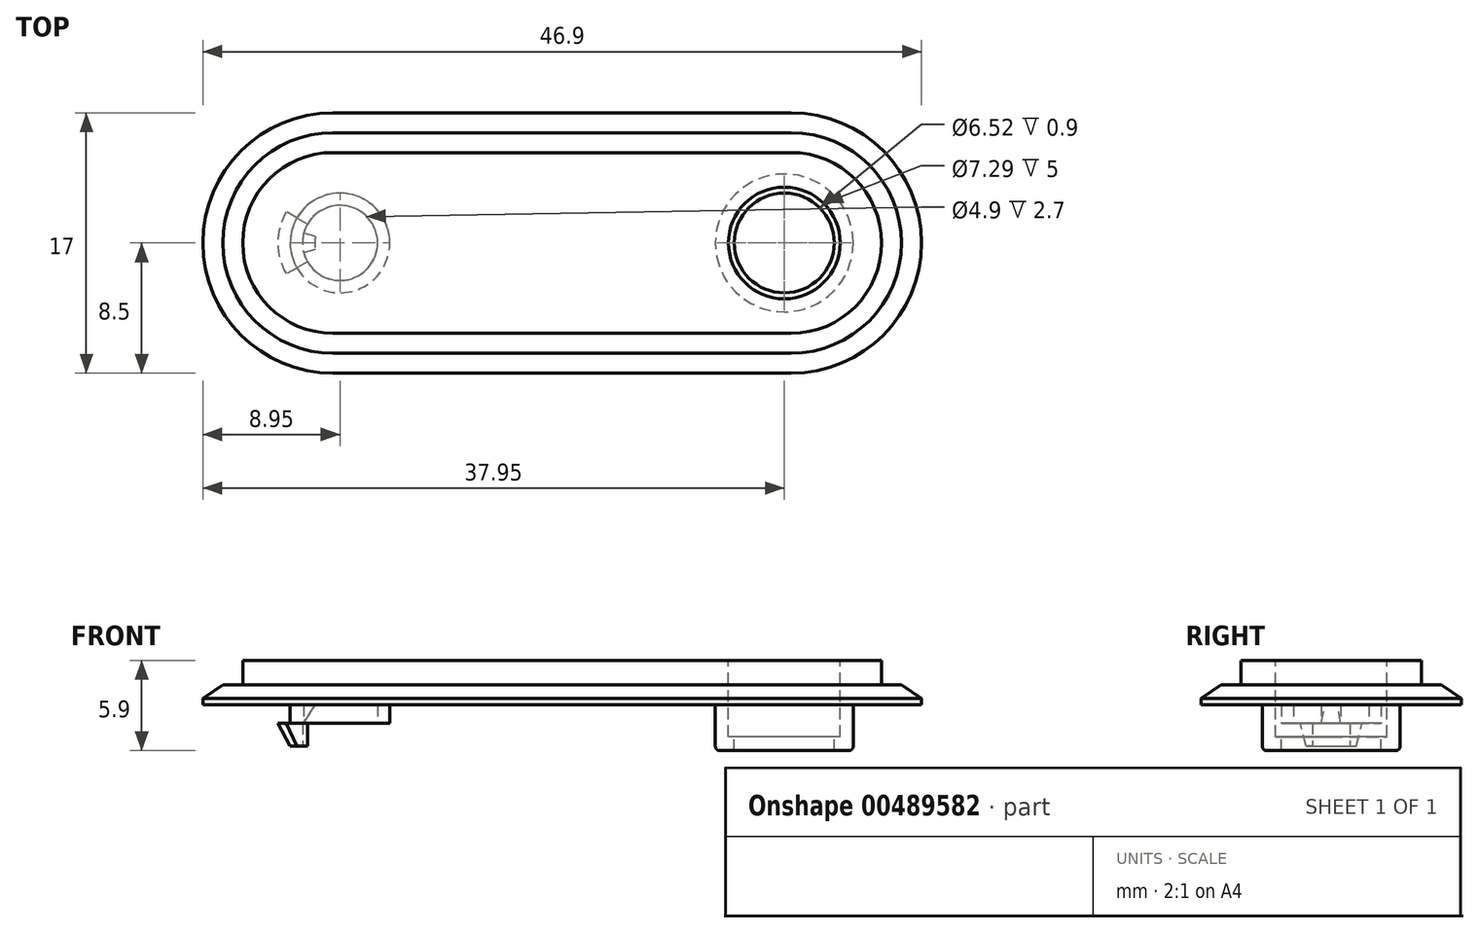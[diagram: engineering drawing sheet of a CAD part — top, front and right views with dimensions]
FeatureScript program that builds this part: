
annotation { "Feature Type Name" : "Feature", "Feature Type Description" : "" }
export const myFeature = defineFeature(function(context is Context, id is Id, definition is map)
    precondition{}
    {
        {
            var Q0;
            Q0=qCreatedBy(makeId("Top.planeOp"),FACE);
            var sketch = newSketch(context, id + "F0", { "sketchPlane" : qUnion([Q0])});
            skLineSegment(sketch, "E0.bottom", {"start": v(-14.95, 5.9) * mm, "end": v(14.95, 5.9) * mm});
            skLineSegment(sketch, "E0.top", {"start": v(-14.95, -5.9) * mm, "end": v(14.95, -5.9) * mm});
            skPoint(sketch, "E0.middle", {"position": v(0, 0) * mm});
            skPoint(sketch, "E1", {"position": v(-14.95, 0) * mm});
            skPoint(sketch, "E2", {"position": v(14.95, 0) * mm});
            skArc(sketch, "E3", {"start": v(-14.95, 5.9) * mm, "mid": v(-20.85, 0) * mm, "end": v(-14.95, -5.9) * mm});
            skArc(sketch, "E4", {"start": v(14.95, -5.9) * mm, "mid": v(20.85, 0) * mm, "end": v(14.95, 5.9) * mm});
            skPoint(sketch, "E5.orphan", {"position": v(-20.85, 5.9) * mm});
            skPoint(sketch, "E6.orphan", {"position": v(-20.85, -5.9) * mm});
            skPoint(sketch, "E7.orphan", {"position": v(20.85, 5.9) * mm});
            skPoint(sketch, "E8.orphan", {"position": v(20.85, -5.9) * mm});
            skPoint(sketch, "E9", {"position": v(-14.5, 0) * mm});
            skPoint(sketch, "E10", {"position": v(14.5, 0) * mm});
            skSolve(sketch);
        }
        {
            var Q0;
            Q0=makeQuery(id+"F0.imprint","IMPRINT",FACE,{"disambiguationData":[TD([[makeQuery(id+"F0.imprint","IMPRINT",EDGE,{"derivedFrom":sQuery(id+"F0.wireOp",EDGE,"E0.bottom")}),-1.0]])]});
            extrude(context, id + "F1", {"entities" : qUnion([Q0]), "depth" : 1.6 * mm});
        }
        {
            var Q0;
            Q0=qCreatedBy(makeId("Top.planeOp"),FACE);
            cPlane(context, id + "F2", {"entities" : qUnion([Q0]), "cplaneType" : CPlaneType.OFFSET, "offset" : 1.3 * mm, "oppositeDirection" : true, "width" : 150 * mm, "height" : 150 * mm});
        }
        {
            var Q0;
            Q0=qCreatedBy(id+"F2.planeOp",FACE);
            var sketch = newSketch(context, id + "F3", { "sketchPlane" : qUnion([Q0])});
            skPoint(sketch, "E11.middle", {"position": v(0, 0) * mm});
            skPoint(sketch, "E12", {"position": v(-14.95, 0) * mm});
            skPoint(sketch, "E13", {"position": v(14.95, 0) * mm});
            skPoint(sketch, "E14.orphan", {"position": v(-20.85, 5.9) * mm});
            skPoint(sketch, "E15.orphan", {"position": v(-20.85, -5.9) * mm});
            skPoint(sketch, "E16.orphan", {"position": v(20.85, 5.9) * mm});
            skPoint(sketch, "E17.orphan", {"position": v(20.85, -5.9) * mm});
            skLineSegment(sketch, "E18.0", {"start": v(-14.95, 8.5) * mm, "end": v(14.95, 8.5) * mm});
            skArc(sketch, "E18.1", {"start": v(-14.95, 8.5) * mm, "mid": v(-23.45, 0) * mm, "end": v(-14.95, -8.5) * mm});
            skLineSegment(sketch, "E18.2", {"start": v(-14.95, -8.5) * mm, "end": v(14.95, -8.5) * mm});
            skArc(sketch, "E18.3", {"start": v(14.95, -8.5) * mm, "mid": v(23.45, 0) * mm, "end": v(14.95, 8.5) * mm});
            skSolve(sketch);
        }
        {
            var Q0;
            Q0 = qSketchRegion(id + "F3", true);
            extrude(context, id + "F4", {"entities" : qUnion([Q0]), "operationType" : NewBodyOperationType.ADD, "depth" : 1.3 * mm});
        }
        {
            var Q0;
            Q0=makeQuery(id+"F4.opExtrude","CAP_EDGE",EDGE,{"disambiguationData":[OSD([sQuery(id+"F3.wireOp",EDGE,"E18.0")])],"isStart":false});
            var Q1;
            Q1=makeQuery(id+"F1.opExtrude","CAP_EDGE",EDGE,{"disambiguationData":[OSD([sQuery(id+"F0.wireOp",EDGE,"E0.top")])],"isStart":true});
            chamfer(context, id + "F5", {"entities" : qUnion([Q0, Q1]), "chamferType" : ChamferType.TWO_OFFSETS, "width1" : 0.9 * mm, "oppositeDirection" : false, "width2" : 1.3 * mm, "tangentPropagation" : true});
        }
        {
            var Q0;
            Q0=makeQuery(id+"F4.opExtrude","CAP_FACE",FACE,{"disambiguationData":[OSD([sQuery(id+"F3.wireOp",EDGE,"E18.0"),sQuery(id+"F3.wireOp",EDGE,"E18.1"),sQuery(id+"F3.wireOp",EDGE,"E18.2"),sQuery(id+"F3.wireOp",EDGE,"E18.3")])],"isStart":true});
            var sketch = newSketch(context, id + "F6", { "sketchPlane" : qUnion([Q0])});
            skCircle(sketch, "E19", {"center": v(14.5, 0) * mm, "radius": 4.5 * mm});
            skCircle(sketch, "E20", {"center": v(14.5, 0) * mm, "radius": 3.26 * mm});
            skSolve(sketch);
        }
        {
            var Q0;
            Q0=makeQuery(id+"F6.imprint","IMPRINT",FACE,{"disambiguationData":[TD([[makeQuery(id+"F6.imprint","IMPRINT",EDGE,{"derivedFrom":sQuery(id+"F6.wireOp",EDGE,"E19")}),1.0]])]});
            extrude(context, id + "F7", {"entities" : qUnion([Q0]), "operationType" : NewBodyOperationType.ADD, "depth" : 3 * mm});
        }
        {
            var Q0;
            Q0=makeQuery(id+"F7.boolean.opBoolean","SPLIT",FACE,{"disambiguationData":[TD([makeQuery(id+"F7.opExtrude","SWEPT_FACE",FACE,{"disambiguationData":[OSD([sQuery(id+"F6.wireOp",EDGE,"E20")])]})])],"derivedFrom":makeQuery(id+"F4.opExtrude","CAP_FACE",FACE,{"disambiguationData":[OSD([sQuery(id+"F3.wireOp",EDGE,"E18.0"),sQuery(id+"F3.wireOp",EDGE,"E18.1"),sQuery(id+"F3.wireOp",EDGE,"E18.2"),sQuery(id+"F3.wireOp",EDGE,"E18.3")])],"isStart":true})});
            extrude(context, id + "F8", {"entities" : qUnion([Q0]), "operationType" : NewBodyOperationType.REMOVE, "endBound" : BoundingType.THROUGH_ALL, "oppositeDirection" : true, "depth" : 25 * mm});
        }
        {
            var Q0;
            Q0=makeQuery(id+"F1.opExtrude","CAP_FACE",FACE,{"disambiguationData":[OSD([sQuery(id+"F0.wireOp",EDGE,"E0.bottom"),sQuery(id+"F0.wireOp",EDGE,"E0.top"),sQuery(id+"F0.wireOp",EDGE,"E3"),sQuery(id+"F0.wireOp",EDGE,"E4")])],"isStart":false});
            var sketch = newSketch(context, id + "F9", { "sketchPlane" : qUnion([Q0])});
            skCircle(sketch, "E21", {"center": v(14.5, 0) * mm, "radius": 3.65 * mm});
            skCircle(sketch, "E22", {"center": v(-14.5, 0) * mm, "radius": 2.45 * mm});
            skSolve(sketch);
        }
        {
            var Q0;
            Q0=makeQuery(id+"F9.imprint","IMPRINT",FACE,{"disambiguationData":[TD([[makeQuery(id+"F9.imprint","IMPRINT",EDGE,{"derivedFrom":sQuery(id+"F9.wireOp",EDGE,"E21")}),1.0]])]});
            extrude(context, id + "F10", {"entities" : qUnion([Q0]), "operationType" : NewBodyOperationType.REMOVE, "oppositeDirection" : true, "depth" : 5 * mm});
        }
        {
            var Q0;
            Q0=qCreatedBy(makeId("Front.planeOp"),FACE);
            var sketch = newSketch(context, id + "F11", { "sketchPlane" : qUnion([Q0])});
            skLineSegment(sketch, "E23", {"start": v(-14.5, 1.6) * mm, "end": v(-14.5, -3.12) * mm, "construction": true});
            skLineSegment(sketch, "E24.bottom", {"start": v(-16.95, -1.3) * mm, "end": v(-17.75, -1.3) * mm});
            skLineSegment(sketch, "E24.top", {"start": v(-16.95, -4) * mm, "end": v(-17.75, -4) * mm});
            skLineSegment(sketch, "E24.left", {"start": v(-16.95, -1.3) * mm, "end": v(-16.95, -4) * mm});
            skLineSegment(sketch, "E24.right", {"start": v(-17.75, -1.3) * mm, "end": v(-17.75, -2.5) * mm});
            skLineSegment(sketch, "E25.top", {"start": v(-16.95, -2.5) * mm, "end": v(-18.55, -2.5) * mm});
            skLineSegment(sketch, "E25.left", {"start": v(-16.95, -4) * mm, "end": v(-16.95, -2.5) * mm});
            skLineSegment(sketch, "E26", {"start": v(-17.75, -4) * mm, "end": v(-18.55, -2.5) * mm});
            skLineSegment(sketch, "E27", {"start": v(-16.95, -2.5) * mm, "end": v(-16.15, -1.3) * mm});
            skLineSegment(sketch, "E28", {"start": v(-16.15, -1.3) * mm, "end": v(-16.95, -1.3) * mm});
            skSolve(sketch);
        }
        {
            var Q0;
            Q0=makeQuery(id+"F11.imprint","IMPRINT",FACE,{"disambiguationData":[TD([[makeQuery(id+"F11.imprint","IMPRINT",EDGE,{"derivedFrom":sQuery(id+"F11.wireOp",EDGE,"E24.bottom")}),1.0]])]});
            var Q1;
            Q1=sQuery(id+"F9.wireOp",EDGE,"E22");
            revolve(context, id + "F12", {"operationType" : NewBodyOperationType.ADD, "entities" : qUnion([Q0]), "axis" : qUnion([Q1]), "revolveType" : RevolveType.FULL});
        }
        {
            var Q0;
            Q0=makeQuery(id+"F11.imprint","IMPRINT",FACE,{"disambiguationData":[TD([[makeQuery(id+"F11.imprint","IMPRINT",EDGE,{"derivedFrom":sQuery(id+"F11.wireOp",EDGE,"E24.top")}),-1.0]])]});
            var Q1;
            Q1=sQuery(id+"F9.wireOp",EDGE,"E22");
            revolve(context, id + "F13", {"operationType" : NewBodyOperationType.ADD, "entities" : qUnion([Q0]), "axis" : qUnion([Q1]), "revolveType" : RevolveType.SYMMETRIC, "angle" : 60 * degree});
        }
        {
            var Q0;
            Q0=makeQuery(id+"F11.imprint","IMPRINT",FACE,{"disambiguationData":[TD([[makeQuery(id+"F11.imprint","IMPRINT",EDGE,{"derivedFrom":sQuery(id+"F11.wireOp",EDGE,"E24.left")}),1.0]])]});
            var Q1;
            Q1=sQuery(id+"F9.wireOp",EDGE,"E22");
            revolve(context, id + "F14", {"operationType" : NewBodyOperationType.ADD, "entities" : qUnion([Q0]), "axis" : qUnion([Q1]), "revolveType" : RevolveType.SYMMETRIC, "angle" : 30 * degree});
        }
        {
            var Q0;
            Q0=makeQuery(id+"F7.opExtrude","CAP_EDGE",EDGE,{"disambiguationData":[OSD([sQuery(id+"F6.wireOp",EDGE,"E19")])],"isStart":false});
            fillet(context, id + "F15", {"entities" : qUnion([Q0]), "radius" : 0.3 * mm, "tangentPropagation" : true, "allowEdgeOverflow" : false});
        }
    });
